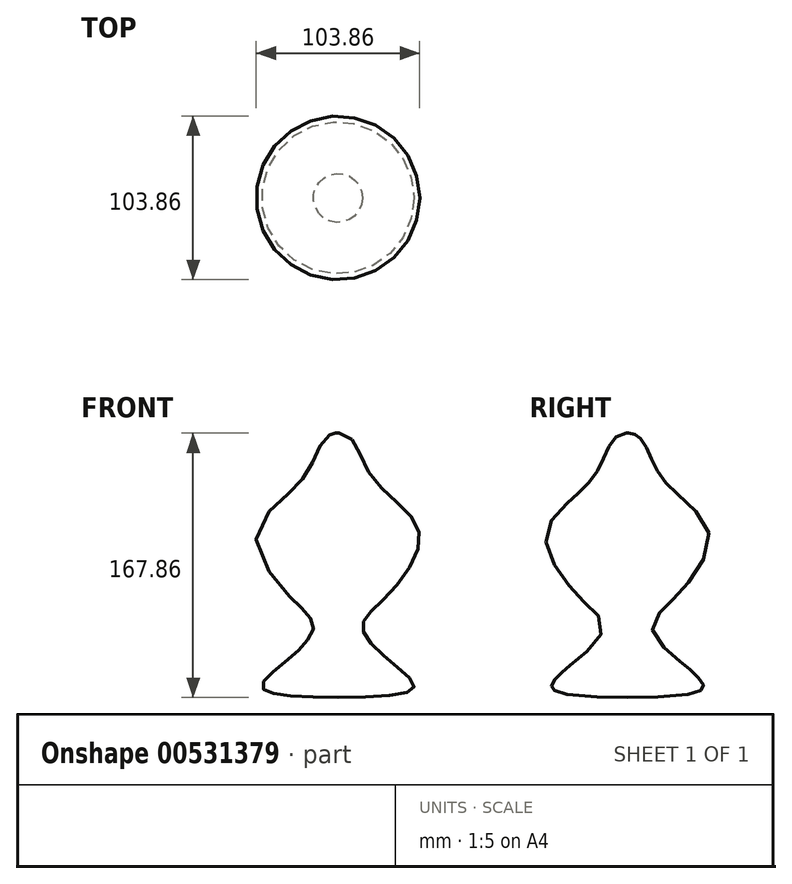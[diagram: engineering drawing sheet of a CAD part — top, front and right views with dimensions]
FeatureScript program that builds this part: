
annotation { "Feature Type Name" : "Feature", "Feature Type Description" : "" }
export const myFeature = defineFeature(function(context is Context, id is Id, definition is map)
    precondition{}
    {
        {
            var Q0;
            Q0=qCreatedBy(makeId("Front.planeOp"),FACE);
            var sketch = newSketch(context, id + "F0", { "sketchPlane" : qUnion([Q0])});
            skLineSegment(sketch, "E0", {"start": v(0, 77.09) * mm, "end": v(0, -90.76) * mm});
            skFitSpline(sketch, "E1", {"points": [v(0, 77.09) * mm, v(20.52, 50.7) * mm, v(51.56, 14.33) * mm, v(30.2, -27.3) * mm, v(15.58, -46.08) * mm, v(33.12, -67.8) * mm, v(48.15, -84.5) * mm, v(0, -90.76) * mm], "startDerivative": vector(254.35, 11.63) * mm, "endDerivative": vector(-407.3, -6.06) * mm});
            skSolve(sketch);
        }
        {
            var Q0;
            Q0 = qSketchRegion(id + "F0", true);
            var Q1;
            Q1=sQuery(id+"F0.wireOp",EDGE,"E0");
            revolve(context, id + "F1", {"entities" : qUnion([Q0]), "axis" : qUnion([Q1]), "revolveType" : RevolveType.FULL});
        }
    });
